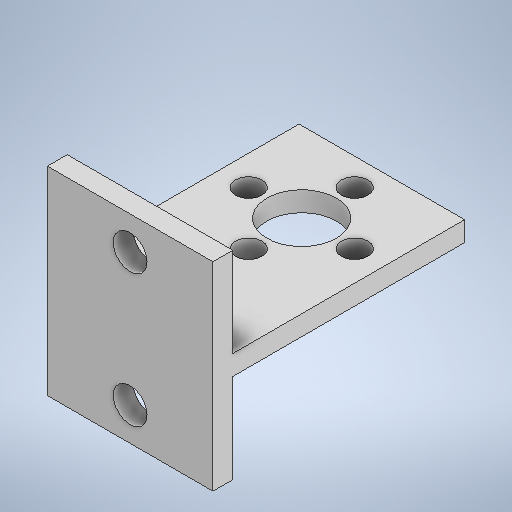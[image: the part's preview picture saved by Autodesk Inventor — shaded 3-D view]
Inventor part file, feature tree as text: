
AUTODESK INVENTOR PART (.ipt)
format: ipt  version: 2025.2 (Build 292293000, 293)  size: 252,928 bytes
history: native  units: mm
features: sketch x5, extrude x4
ambient origin geometry x8: Origin, YZ Plane, XZ Plane, XY Plane, X Axis, Y Axis, Z Axis, Center Point
bodies: Solid1 (feature_tree)
feature tree (9):
  extrude  "Extrusion1"  Depth=30.0mm
  extrude  "Extrusion2"  Depth=3.0mm
  extrude  "Extrusion3"  Depth=35.0mm
  extrude  "Extrusion4"  Depth=5.1mm
  sketch  "Sketch1"  dims[d0=25.0mm d1=30.0mm]
  sketch  "Sketch2"  dims[d5=35.0mm d6=0.0mm d7=20.0mm]
  sketch  "Sketch3"  dims[d8=5.1mm d9=5.1mm]
  sketch  "Sketch4"  dims[d10=0.0mm d11=0.0mm d12=22.896mm d13=10.5mm d14=16.0mm d15=4.0mm d16=40.0mm d18=360.0deg d20=0.0mm d21=0.0mm]
  sketch  "Sketch Circular Pattern1"  dims[d2=3.0mm d3=0.0mm d4=3.0mm]
